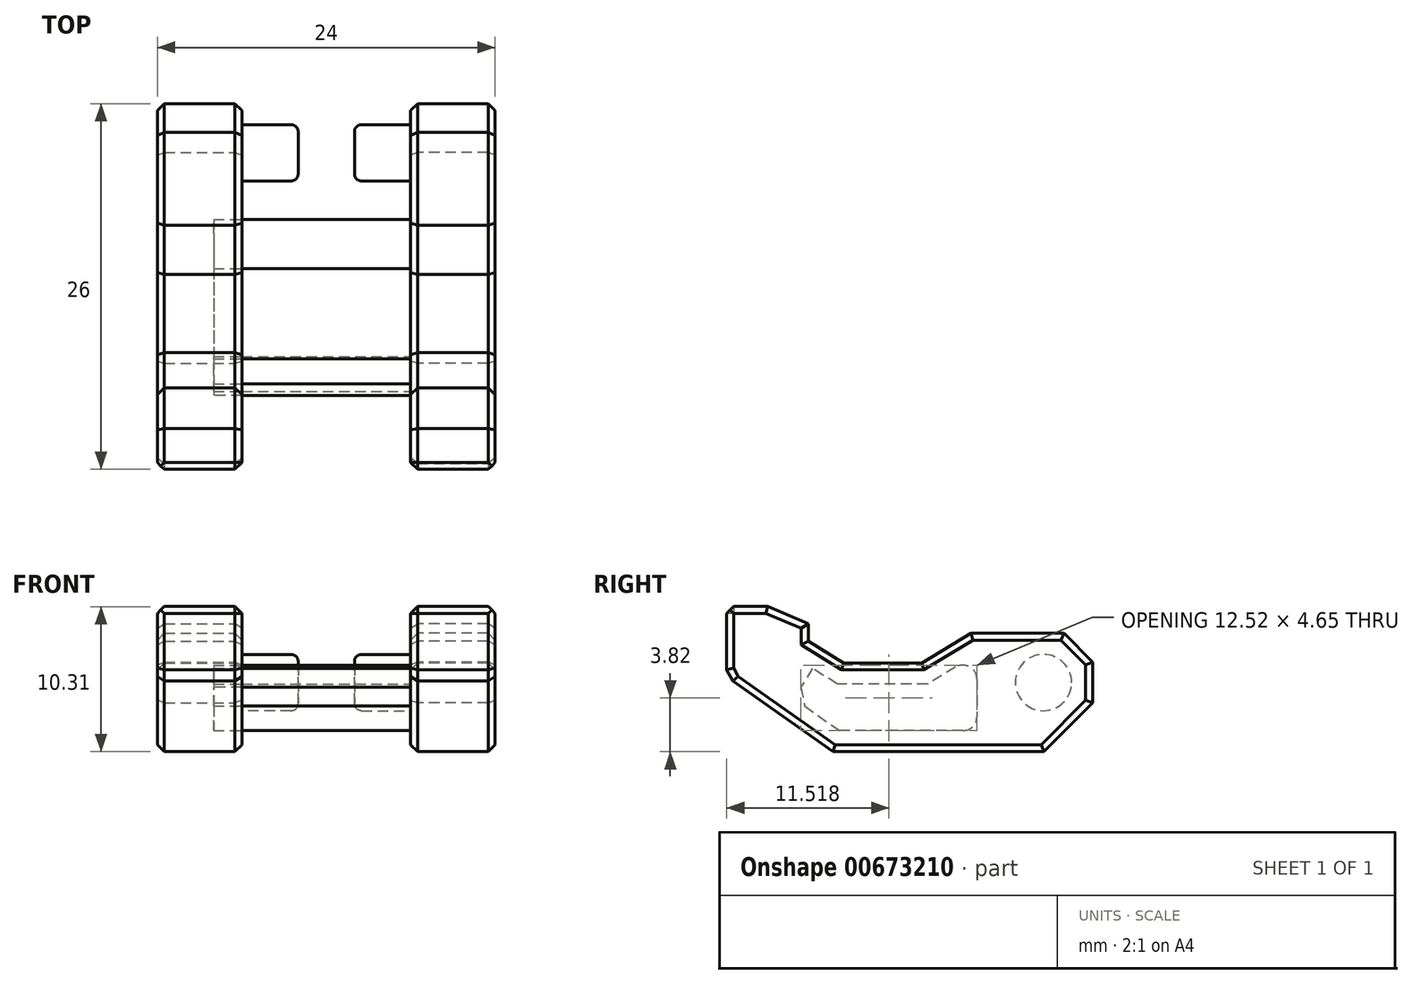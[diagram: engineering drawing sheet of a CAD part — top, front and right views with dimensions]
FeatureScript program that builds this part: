
annotation { "Feature Type Name" : "Feature", "Feature Type Description" : "" }
export const myFeature = defineFeature(function(context is Context, id is Id, definition is map)
    precondition{}
    {
        {
            var Q0;
            Q0=qCreatedBy(makeId("Right.planeOp"),FACE);
            var sketch = newSketch(context, id + "F0", { "sketchPlane" : qUnion([Q0])});
            skCircle(sketch, "E0", {"center": v(0, 0) * mm, "radius": 2 * mm});
            skArc(sketch, "E1.cCircle", {"start": v(2.47, -2.47) * mm, "mid": v(3.23, 1.34) * mm, "end": v(0, 3.5) * mm, "construction": true});
            skLineSegment(sketch, "E1.0", {"start": v(-1.45, 3.5) * mm, "end": v(1.45, 3.5) * mm});
            skLineSegment(sketch, "E1.1", {"start": v(1.45, 3.5) * mm, "end": v(3.5, 1.45) * mm});
            skLineSegment(sketch, "E1.2", {"start": v(3.5, 1.45) * mm, "end": v(3.5, -1.45) * mm});
            skLineSegment(sketch, "E1.3", {"start": v(3.5, -1.45) * mm, "end": v(1.45, -3.5) * mm});
            skPoint(sketch, "E1.0.midPoint", {"position": v(0, 3.5) * mm});
            skLineSegment(sketch, "E2", {"start": v(-1.45, 3.5) * mm, "end": v(-5.14, 3.5) * mm});
            skLineSegment(sketch, "E3", {"start": v(-5.14, 3.5) * mm, "end": v(-8.64, 1.4) * mm});
            skLineSegment(sketch, "E4", {"start": v(-16.7, 2.95) * mm, "end": v(-16.7, 4.18) * mm});
            skLineSegment(sketch, "E5", {"start": v(-19.6, 5.4) * mm, "end": v(-22.5, 5.4) * mm});
            skLineSegment(sketch, "E6", {"start": v(-22.5, 5.4) * mm, "end": v(-22.5, 0.4) * mm});
            skLineSegment(sketch, "E7", {"start": v(-22.5, 0.4) * mm, "end": v(-16.97, -3.5) * mm});
            skLineSegment(sketch, "E8", {"start": v(-11.14, 1.4) * mm, "end": v(-14.2, 1.4) * mm});
            skLineSegment(sketch, "E9", {"start": v(-14.2, 1.4) * mm, "end": v(-16.7, 2.95) * mm});
            skLineSegment(sketch, "E10", {"start": v(-11.14, 1.4) * mm, "end": v(-8.64, 1.4) * mm});
            skLineSegment(sketch, "E11", {"start": v(1.45, -3.5) * mm, "end": v(0.04, -4.91) * mm});
            skLineSegment(sketch, "E12", {"start": v(0.04, -4.91) * mm, "end": v(-14.96, -4.91) * mm});
            skLineSegment(sketch, "E13", {"start": v(-16.97, -3.5) * mm, "end": v(-14.96, -4.91) * mm});
            skLineSegment(sketch, "E14.2", {"start": v(-17.74, -1.12) * mm, "end": v(-16.1, -2.27) * mm});
            skLineSegment(sketch, "E14.3", {"start": v(-16.1, -2.27) * mm, "end": v(-14.49, -3.41) * mm});
            skLineSegment(sketch, "E14.4", {"start": v(-5.72, -3.41) * mm, "end": v(-14.49, -3.41) * mm});
            skLineSegment(sketch, "E14.7", {"start": v(-14.63, -0.1) * mm, "end": v(-16.41, 1) * mm});
            skLineSegment(sketch, "E14.8", {"start": v(-11.14, -0.1) * mm, "end": v(-14.63, -0.1) * mm});
            skLineSegment(sketch, "E14.9", {"start": v(-11.14, -0.1) * mm, "end": v(-8.23, -0.1) * mm});
            skLineSegment(sketch, "E14.10", {"start": v(-6.24, 1.1) * mm, "end": v(-8.23, -0.1) * mm});
            skLineSegment(sketch, "E15", {"start": v(-16.41, 1) * mm, "end": v(-17.74, -1.12) * mm});
            skPoint(sketch, "E14.6.start.orphan", {"position": v(-18.2, 2.12) * mm});
            skLineSegment(sketch, "E16", {"start": v(-4.72, 0.23) * mm, "end": v(-4.72, -2.41) * mm});
            skPoint(sketch, "E17.visualSharp", {"position": v(-4.72, 2) * mm});
            skArc(sketch, "E17.filletArc", {"start": v(-4.72, 0.23) * mm, "mid": v(-5.23, 1.1) * mm, "end": v(-6.24, 1.1) * mm});
            skPoint(sketch, "E18.visualSharp", {"position": v(-4.72, -3.41) * mm});
            skArc(sketch, "E18.filletArc", {"start": v(-5.72, -3.41) * mm, "mid": v(-5.02, -3.12) * mm, "end": v(-4.72, -2.41) * mm});
            skLineSegment(sketch, "E19", {"start": v(-16.7, 4.18) * mm, "end": v(-19.6, 5.4) * mm});
            skPoint(sketch, "E20.orphan", {"position": v(-16.7, 5.4) * mm});
            skSolve(sketch);
        }
        {
            var Q0;
            Q0=makeQuery(id+"F0.imprint","IMPRINT",FACE,{"disambiguationData":[TD([[makeQuery(id+"F0.imprint","IMPRINT",EDGE,{"derivedFrom":sQuery(id+"F0.wireOp",EDGE,"E0")}),1.0]])]});
            var Q1;
            Q1=makeQuery(id+"F0.imprint","IMPRINT",FACE,{"disambiguationData":[TD([[makeQuery(id+"F0.imprint","IMPRINT",EDGE,{"derivedFrom":sQuery(id+"F0.wireOp",EDGE,"E0")}),-1.0]])]});
            var Q2;
            Q2=makeQuery(id+"F0.imprint","IMPRINT",FACE,{"disambiguationData":[TD([[makeQuery(id+"F0.imprint","IMPRINT",EDGE,{"derivedFrom":sQuery(id+"F0.wireOp",EDGE,"E14.2")}),1.0]])]});
            extrude(context, id + "F1", {"entities" : qUnion([Q0, Q1, Q2]), "oppositeDirection" : true, "depth" : 6 * mm});
        }
        {
            var Q0;
            Q0=makeQuery(id+"F0.imprint","IMPRINT",FACE,{"disambiguationData":[TD([[makeQuery(id+"F0.imprint","IMPRINT",EDGE,{"derivedFrom":sQuery(id+"F0.wireOp",EDGE,"E0")}),1.0]])]});
            var Q1;
            Q1=sQuery(id+"F0.wireOp",EDGE,"E0");
            extrude(context, id + "F2", {"entities" : qUnion([Q0]), "operationType" : NewBodyOperationType.ADD, "surfaceEntities" : qUnion([Q1]), "depth" : 4 * mm});
        }
        {
            var Q0;
            Q0=makeQuery(id+"F0.imprint","IMPRINT",FACE,{"disambiguationData":[TD([[makeQuery(id+"F0.imprint","IMPRINT",EDGE,{"derivedFrom":sQuery(id+"F0.wireOp",EDGE,"E14.2")}),1.0]])]});
            extrude(context, id + "F3", {"entities" : qUnion([Q0]), "operationType" : NewBodyOperationType.REMOVE, "oppositeDirection" : true, "depth" : 2 * mm});
        }
        {
            var Q0;
            Q0=makeQuery(id+"F3.boolean.opBoolean","COPY",EDGE,{"derivedFrom":makeQuery(id+"F3.opExtrude","SWEPT_EDGE",EDGE,{"disambiguationData":[OSD([sQuery(id+"F0.wireOp",EDGE,"E14.2"),sQuery(id+"F0.wireOp",EDGE,"E15")])]})});
            chamfer(context, id + "F4", {"entities" : qUnion([Q0]), "width" : 1 * mm, "tangentPropagation" : true});
        }
        {
            var Q0;
            Q0=makeQuery(id+"F1.opExtrude","SWEPT_EDGE",EDGE,{"disambiguationData":[OSD([sQuery(id+"F0.wireOp",EDGE,"E6"),sQuery(id+"F0.wireOp",EDGE,"E7")])]});
            chamfer(context, id + "F5", {"entities" : qUnion([Q0]), "width" : 1 * mm, "tangentPropagation" : true});
        }
        {
            var Q0;
            Q0=makeQuery(id+"F1.opExtrude","CAP_EDGE",EDGE,{"disambiguationData":[OSD([sQuery(id+"F0.wireOp",EDGE,"E5")])],"isStart":false});
            var Q1;
            Q1=makeQuery(id+"F1.opExtrude","CAP_EDGE",EDGE,{"disambiguationData":[OSD([sQuery(id+"F0.wireOp",EDGE,"E9")])],"isStart":false});
            var Q2;
            Q2=makeQuery(id+"F1.opExtrude","CAP_EDGE",EDGE,{"disambiguationData":[OSD([sQuery(id+"F0.wireOp",EDGE,"E8"),sQuery(id+"F0.wireOp",EDGE,"E10")])],"isStart":false});
            var Q3;
            Q3=makeQuery(id+"F1.opExtrude","CAP_EDGE",EDGE,{"disambiguationData":[OSD([sQuery(id+"F0.wireOp",EDGE,"E3")])],"isStart":false});
            var Q4;
            Q4=makeQuery(id+"F1.opExtrude","CAP_EDGE",EDGE,{"disambiguationData":[OSD([sQuery(id+"F0.wireOp",EDGE,"E1.0"),sQuery(id+"F0.wireOp",EDGE,"E2")])],"isStart":false});
            var Q5;
            {var subQ0=sQuery(id+"F0.wireOp",EDGE,"E7");var subQ1=sQuery(id+"F0.wireOp",EDGE,"E6");Q5=makeQuery(id+"F5.opChamfer","BLEND_EDGE",EDGE,{"blendedFrom":[makeQuery(id+"F1.opExtrude","SWEPT_EDGE",EDGE,{"disambiguationData":[OSD([subQ1,subQ0])]}),makeQuery(id+"F1.opExtrude","CAP_FACE",FACE,{"disambiguationData":[OSD([sQuery(id+"F0.wireOp",EDGE,"E1.0"),sQuery(id+"F0.wireOp",EDGE,"E1.1"),sQuery(id+"F0.wireOp",EDGE,"E1.2"),sQuery(id+"F0.wireOp",EDGE,"E1.3"),sQuery(id+"F0.wireOp",EDGE,"E2"),sQuery(id+"F0.wireOp",EDGE,"E3"),sQuery(id+"F0.wireOp",EDGE,"E4"),sQuery(id+"F0.wireOp",EDGE,"E5"),subQ1,subQ0,sQuery(id+"F0.wireOp",EDGE,"E8"),sQuery(id+"F0.wireOp",EDGE,"E9"),sQuery(id+"F0.wireOp",EDGE,"E10"),sQuery(id+"F0.wireOp",EDGE,"E11"),sQuery(id+"F0.wireOp",EDGE,"E12"),sQuery(id+"F0.wireOp",EDGE,"E13")])],"isStart":false})],"blendedInto":[makeQuery(id+"F1.opExtrude","CAP_FACE",FACE,{"disambiguationData":[OSD([sQuery(id+"F0.wireOp",EDGE,"E1.0"),sQuery(id+"F0.wireOp",EDGE,"E1.1"),sQuery(id+"F0.wireOp",EDGE,"E1.2"),sQuery(id+"F0.wireOp",EDGE,"E1.3"),sQuery(id+"F0.wireOp",EDGE,"E2"),sQuery(id+"F0.wireOp",EDGE,"E3"),sQuery(id+"F0.wireOp",EDGE,"E4"),sQuery(id+"F0.wireOp",EDGE,"E5"),subQ1,subQ0,sQuery(id+"F0.wireOp",EDGE,"E8"),sQuery(id+"F0.wireOp",EDGE,"E9"),sQuery(id+"F0.wireOp",EDGE,"E10"),sQuery(id+"F0.wireOp",EDGE,"E11"),sQuery(id+"F0.wireOp",EDGE,"E12"),sQuery(id+"F0.wireOp",EDGE,"E13")])],"isStart":false})]});}
            var Q6;
            Q6=makeQuery(id+"F1.opExtrude","CAP_EDGE",EDGE,{"disambiguationData":[OSD([sQuery(id+"F0.wireOp",EDGE,"E7"),sQuery(id+"F0.wireOp",EDGE,"E13")])],"isStart":false});
            var Q7;
            Q7=makeQuery(id+"F1.opExtrude","CAP_EDGE",EDGE,{"disambiguationData":[OSD([sQuery(id+"F0.wireOp",EDGE,"E6")])],"isStart":false});
            var Q8;
            Q8=makeQuery(id+"F1.opExtrude","CAP_EDGE",EDGE,{"disambiguationData":[OSD([sQuery(id+"F0.wireOp",EDGE,"E1.1")])],"isStart":false});
            var Q9;
            Q9=makeQuery(id+"F1.opExtrude","CAP_EDGE",EDGE,{"disambiguationData":[OSD([sQuery(id+"F0.wireOp",EDGE,"E1.2")])],"isStart":false});
            var Q10;
            Q10=makeQuery(id+"F1.opExtrude","CAP_EDGE",EDGE,{"disambiguationData":[OSD([sQuery(id+"F0.wireOp",EDGE,"E1.3"),sQuery(id+"F0.wireOp",EDGE,"E11")])],"isStart":false});
            var Q11;
            Q11=makeQuery(id+"F1.opExtrude","CAP_EDGE",EDGE,{"disambiguationData":[OSD([sQuery(id+"F0.wireOp",EDGE,"E4")])],"isStart":false});
            var Q12;
            Q12=makeQuery(id+"F1.opExtrude","CAP_EDGE",EDGE,{"disambiguationData":[OSD([sQuery(id+"F0.wireOp",EDGE,"E12")])],"isStart":false});
            var Q13;
            Q13=makeQuery(id+"F1.opExtrude","CAP_EDGE",EDGE,{"disambiguationData":[OSD([sQuery(id+"F0.wireOp",EDGE,"E19")])],"isStart":false});
            var Q14;
            Q14=makeQuery(id+"F1.opExtrude","CAP_EDGE",EDGE,{"disambiguationData":[OSD([sQuery(id+"F0.wireOp",EDGE,"E19")])],"isStart":true});
            chamfer(context, id + "F6", {"entities" : qUnion([Q0, Q1, Q2, Q3, Q4, Q5, Q6, Q7, Q8, Q9, Q10, Q11, Q12, Q13, Q14]), "width" : .5 * mm, "tangentPropagation" : true});
        }
        {
            var Q0;
            Q0=makeQuery(id+"F1.opExtrude","CAP_EDGE",EDGE,{"disambiguationData":[OSD([sQuery(id+"F0.wireOp",EDGE,"E8"),sQuery(id+"F0.wireOp",EDGE,"E10")])],"isStart":true});
            var Q1;
            Q1=makeQuery(id+"F1.opExtrude","CAP_EDGE",EDGE,{"disambiguationData":[OSD([sQuery(id+"F0.wireOp",EDGE,"E3")])],"isStart":true});
            var Q2;
            Q2=makeQuery(id+"F1.opExtrude","CAP_EDGE",EDGE,{"disambiguationData":[OSD([sQuery(id+"F0.wireOp",EDGE,"E9")])],"isStart":true});
            var Q3;
            Q3=makeQuery(id+"F1.opExtrude","CAP_EDGE",EDGE,{"disambiguationData":[OSD([sQuery(id+"F0.wireOp",EDGE,"E4")])],"isStart":true});
            var Q4;
            Q4=makeQuery(id+"F1.opExtrude","CAP_EDGE",EDGE,{"disambiguationData":[OSD([sQuery(id+"F0.wireOp",EDGE,"E5")])],"isStart":true});
            var Q5;
            Q5=makeQuery(id+"F1.opExtrude","CAP_EDGE",EDGE,{"disambiguationData":[OSD([sQuery(id+"F0.wireOp",EDGE,"E6")])],"isStart":true});
            var Q6;
            {var subQ0=sQuery(id+"F0.wireOp",EDGE,"E7");var subQ1=sQuery(id+"F0.wireOp",EDGE,"E6");Q6=makeQuery(id+"F5.opChamfer","BLEND_EDGE",EDGE,{"blendedFrom":[makeQuery(id+"F1.opExtrude","SWEPT_EDGE",EDGE,{"disambiguationData":[OSD([subQ1,subQ0])]}),makeQuery(id+"F1.opExtrude","CAP_FACE",FACE,{"disambiguationData":[OSD([sQuery(id+"F0.wireOp",EDGE,"E1.0"),sQuery(id+"F0.wireOp",EDGE,"E1.1"),sQuery(id+"F0.wireOp",EDGE,"E1.2"),sQuery(id+"F0.wireOp",EDGE,"E1.3"),sQuery(id+"F0.wireOp",EDGE,"E2"),sQuery(id+"F0.wireOp",EDGE,"E3"),sQuery(id+"F0.wireOp",EDGE,"E4"),sQuery(id+"F0.wireOp",EDGE,"E5"),subQ1,subQ0,sQuery(id+"F0.wireOp",EDGE,"E8"),sQuery(id+"F0.wireOp",EDGE,"E9"),sQuery(id+"F0.wireOp",EDGE,"E10"),sQuery(id+"F0.wireOp",EDGE,"E11"),sQuery(id+"F0.wireOp",EDGE,"E12"),sQuery(id+"F0.wireOp",EDGE,"E13")])],"isStart":true})],"blendedInto":[makeQuery(id+"F1.opExtrude","CAP_FACE",FACE,{"disambiguationData":[OSD([sQuery(id+"F0.wireOp",EDGE,"E1.0"),sQuery(id+"F0.wireOp",EDGE,"E1.1"),sQuery(id+"F0.wireOp",EDGE,"E1.2"),sQuery(id+"F0.wireOp",EDGE,"E1.3"),sQuery(id+"F0.wireOp",EDGE,"E2"),sQuery(id+"F0.wireOp",EDGE,"E3"),sQuery(id+"F0.wireOp",EDGE,"E4"),sQuery(id+"F0.wireOp",EDGE,"E5"),subQ1,subQ0,sQuery(id+"F0.wireOp",EDGE,"E8"),sQuery(id+"F0.wireOp",EDGE,"E9"),sQuery(id+"F0.wireOp",EDGE,"E10"),sQuery(id+"F0.wireOp",EDGE,"E11"),sQuery(id+"F0.wireOp",EDGE,"E12"),sQuery(id+"F0.wireOp",EDGE,"E13")])],"isStart":true})]});}
            var Q7;
            Q7=makeQuery(id+"F1.opExtrude","CAP_EDGE",EDGE,{"disambiguationData":[OSD([sQuery(id+"F0.wireOp",EDGE,"E7"),sQuery(id+"F0.wireOp",EDGE,"E13")])],"isStart":true});
            var Q8;
            Q8=makeQuery(id+"F1.opExtrude","CAP_EDGE",EDGE,{"disambiguationData":[OSD([sQuery(id+"F0.wireOp",EDGE,"E12")])],"isStart":true});
            var Q9;
            Q9=makeQuery(id+"F1.opExtrude","CAP_EDGE",EDGE,{"disambiguationData":[OSD([sQuery(id+"F0.wireOp",EDGE,"E1.3"),sQuery(id+"F0.wireOp",EDGE,"E11")])],"isStart":true});
            var Q10;
            Q10=makeQuery(id+"F1.opExtrude","CAP_EDGE",EDGE,{"disambiguationData":[OSD([sQuery(id+"F0.wireOp",EDGE,"E1.2")])],"isStart":true});
            var Q11;
            Q11=makeQuery(id+"F1.opExtrude","CAP_EDGE",EDGE,{"disambiguationData":[OSD([sQuery(id+"F0.wireOp",EDGE,"E1.1")])],"isStart":true});
            var Q12;
            Q12=makeQuery(id+"F1.opExtrude","CAP_EDGE",EDGE,{"disambiguationData":[OSD([sQuery(id+"F0.wireOp",EDGE,"E1.0"),sQuery(id+"F0.wireOp",EDGE,"E2")])],"isStart":true});
            var Q13;
            Q13=makeQuery(id+"F1.opExtrude","SWEPT_EDGE",EDGE,{"disambiguationData":[OSD([sQuery(id+"F0.wireOp",EDGE,"E5"),sQuery(id+"F0.wireOp",EDGE,"E6")])]});
            chamfer(context, id + "F7", {"entities" : qUnion([Q0, Q1, Q2, Q3, Q4, Q5, Q6, Q7, Q8, Q9, Q10, Q11, Q12, Q13]), "width" : .5 * mm, "tangentPropagation" : true});
        }
        {
            var Q0;
            Q0=makeQuery(id+"F2.opExtrude","CAP_FACE",FACE,{"disambiguationData":[OSD([sQuery(id+"F0.wireOp",EDGE,"E0")])],"isStart":false});
            fillet(context, id + "F8", {"entities" : qUnion([Q0]), "radius" : .5 * mm, "tangentPropagation" : true, "allowEdgeOverflow" : false});
        }
        {
            var Q0;
            Q0=qCreatedBy(makeId("Right.planeOp"),FACE);
            cPlane(context, id + "F9", {"entities" : qUnion([Q0]), "cplaneType" : CPlaneType.OFFSET, "offset" : 6 * mm, "width" : 150 * mm, "height" : 150 * mm});
        }
        {
            var Q0;
            Q0=makeQuery(id+"F1.opExtrude","SWEPT_BODY",BODY,{"disambiguationData":[OSD([sQuery(id+"F0.wireOp",EDGE,"E1.0"),sQuery(id+"F0.wireOp",EDGE,"E1.1"),sQuery(id+"F0.wireOp",EDGE,"E1.2"),sQuery(id+"F0.wireOp",EDGE,"E1.3"),sQuery(id+"F0.wireOp",EDGE,"E2"),sQuery(id+"F0.wireOp",EDGE,"E3"),sQuery(id+"F0.wireOp",EDGE,"E4"),sQuery(id+"F0.wireOp",EDGE,"E5"),sQuery(id+"F0.wireOp",EDGE,"E6"),sQuery(id+"F0.wireOp",EDGE,"E7"),sQuery(id+"F0.wireOp",EDGE,"E8"),sQuery(id+"F0.wireOp",EDGE,"E9"),sQuery(id+"F0.wireOp",EDGE,"E10"),sQuery(id+"F0.wireOp",EDGE,"E11"),sQuery(id+"F0.wireOp",EDGE,"E12"),sQuery(id+"F0.wireOp",EDGE,"E13")])]});
            var Q1;
            Q1=qCreatedBy(id+"F9.planeOp",FACE);
            mirror(context, id + "F10", {"entities" : qUnion([Q0]), "mirrorPlane" : qUnion([Q1])});
        }
        {
            var Q0;
            Q0=makeQuery(id+"F10.opPattern","COPY",FACE,{"derivedFrom":makeQuery(id+"F3.boolean.opBoolean","COPY",FACE,{"derivedFrom":makeQuery(id+"F3.opExtrude","CAP_FACE",FACE,{"disambiguationData":[OSD([sQuery(id+"F0.wireOp",EDGE,"E14.2"),sQuery(id+"F0.wireOp",EDGE,"E14.3"),sQuery(id+"F0.wireOp",EDGE,"E14.4"),sQuery(id+"F0.wireOp",EDGE,"E14.7"),sQuery(id+"F0.wireOp",EDGE,"E14.8"),sQuery(id+"F0.wireOp",EDGE,"E14.9"),sQuery(id+"F0.wireOp",EDGE,"E14.10"),sQuery(id+"F0.wireOp",EDGE,"E15"),sQuery(id+"F0.wireOp",EDGE,"E16"),sQuery(id+"F0.wireOp",EDGE,"E17.filletArc"),sQuery(id+"F0.wireOp",EDGE,"E18.filletArc")])],"isStart":false})}),"instanceName":"1"});
            extrude(context, id + "F11", {"entities" : qUnion([Q0]), "operationType" : NewBodyOperationType.ADD, "depth" : 14 * mm});
        }
    });
